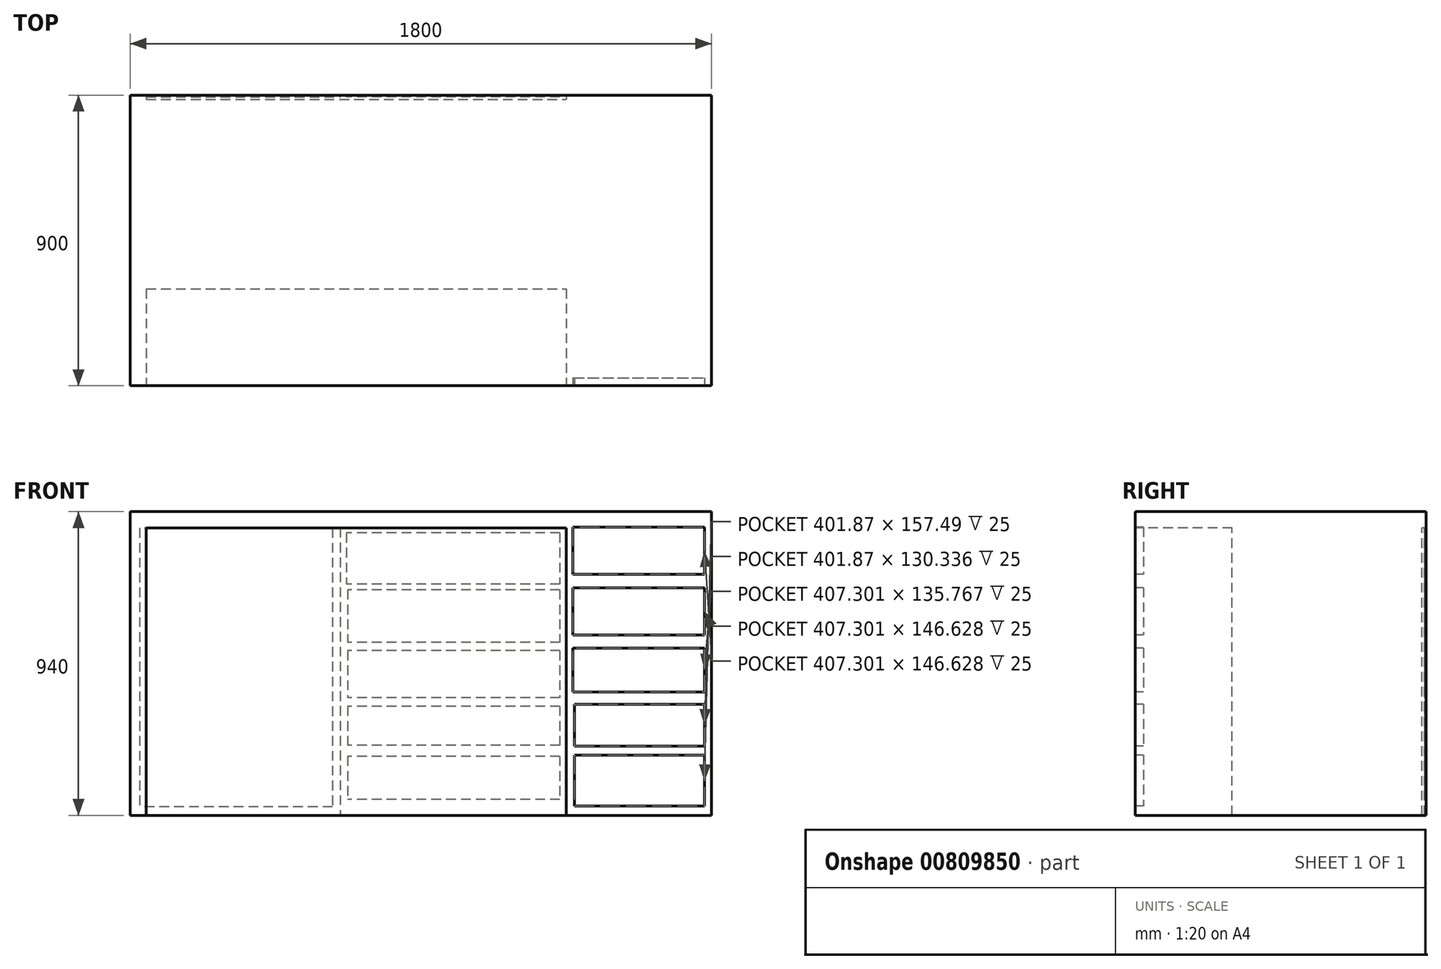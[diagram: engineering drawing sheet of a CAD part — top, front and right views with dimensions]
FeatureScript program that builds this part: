
annotation { "Feature Type Name" : "Feature", "Feature Type Description" : "" }
export const myFeature = defineFeature(function(context is Context, id is Id, definition is map)
    precondition{}
    {
        {
            var Q0;
            Q0=qCreatedBy(makeId("Front.planeOp"),FACE);
            var sketch = newSketch(context, id + "F0", { "sketchPlane" : qUnion([Q0])});
            skLineSegment(sketch, "E0.bottom", {"start": v(0, 0) * mm, "end": v(50, 0) * mm});
            skLineSegment(sketch, "E0.top", {"start": v(0, 940) * mm, "end": v(1800, 940) * mm});
            skLineSegment(sketch, "E0.left", {"start": v(0, 0) * mm, "end": v(0, 940) * mm});
            skLineSegment(sketch, "E0.right", {"start": v(1800, 0) * mm, "end": v(1800, 940) * mm});
            skLineSegment(sketch, "E1", {"start": v(50, 0) * mm, "end": v(50, 890) * mm});
            skLineSegment(sketch, "E2", {"start": v(50, 890) * mm, "end": v(1350, 890) * mm});
            skLineSegment(sketch, "E3", {"start": v(1350, 890) * mm, "end": v(1350, 0) * mm});
            skLineSegment(sketch, "E4.trimOffspring", {"start": v(1350, 0) * mm, "end": v(1800, 0) * mm});
            skSolve(sketch);
        }
        {
            var Q0;
            Q0 = qSketchRegion(id + "F0", true);
            extrude(context, id + "F1", {"entities" : qUnion([Q0]), "oppositeDirection" : true, "depth" : 900 * mm, "offsetDistance" : 25 * mm});
        }
        {
            var Q0;
            Q0=makeQuery(id+"F1.opExtrude","CAP_FACE",FACE,{"disambiguationData":[OSD([sQuery(id+"F0.wireOp",EDGE,"E0.bottom"),sQuery(id+"F0.wireOp",EDGE,"E0.top"),sQuery(id+"F0.wireOp",EDGE,"E0.left"),sQuery(id+"F0.wireOp",EDGE,"E0.right"),sQuery(id+"F0.wireOp",EDGE,"E1"),sQuery(id+"F0.wireOp",EDGE,"E2"),sQuery(id+"F0.wireOp",EDGE,"E3"),sQuery(id+"F0.wireOp",EDGE,"E4.trimOffspring")])],"isStart":true});
            var sketch = newSketch(context, id + "F2", { "sketchPlane" : qUnion([Q0])});
            skLineSegment(sketch, "E5.bottom", {"start": v(1370.64, 892.35) * mm, "end": v(1777.94, 892.35) * mm});
            skLineSegment(sketch, "E5.top", {"start": v(1370.64, 745.72) * mm, "end": v(1777.94, 745.72) * mm});
            skLineSegment(sketch, "E5.left", {"start": v(1370.64, 892.35) * mm, "end": v(1370.64, 745.72) * mm});
            skLineSegment(sketch, "E5.right", {"start": v(1777.94, 892.35) * mm, "end": v(1777.94, 745.72) * mm});
            skLineSegment(sketch, "E6.bottom", {"start": v(1370.64, 705) * mm, "end": v(1777.94, 705) * mm});
            skLineSegment(sketch, "E6.top", {"start": v(1370.64, 558.36) * mm, "end": v(1777.94, 558.36) * mm});
            skLineSegment(sketch, "E6.left", {"start": v(1370.64, 705) * mm, "end": v(1370.64, 558.36) * mm});
            skLineSegment(sketch, "E6.right", {"start": v(1777.94, 705) * mm, "end": v(1777.94, 558.36) * mm});
            skPoint(sketch, "E7.firstSnap0", {"position": v(1370.64, 631.68) * mm});
            skLineSegment(sketch, "E7.bottom", {"start": v(1370.64, 517.63) * mm, "end": v(1777.94, 517.63) * mm});
            skLineSegment(sketch, "E7.top", {"start": v(1370.64, 381.87) * mm, "end": v(1777.94, 381.87) * mm});
            skLineSegment(sketch, "E7.left", {"start": v(1370.64, 517.63) * mm, "end": v(1370.64, 381.87) * mm});
            skLineSegment(sketch, "E7.right", {"start": v(1777.94, 517.63) * mm, "end": v(1777.94, 381.87) * mm});
            skLineSegment(sketch, "E8.bottom", {"start": v(1376.07, 343.85) * mm, "end": v(1777.94, 343.85) * mm});
            skLineSegment(sketch, "E8.top", {"start": v(1376.07, 213.51) * mm, "end": v(1777.94, 213.51) * mm});
            skLineSegment(sketch, "E8.left", {"start": v(1376.07, 343.85) * mm, "end": v(1376.07, 213.51) * mm});
            skLineSegment(sketch, "E8.right", {"start": v(1777.94, 343.85) * mm, "end": v(1777.94, 213.51) * mm});
            skLineSegment(sketch, "E9.bottom", {"start": v(1376.07, 186.36) * mm, "end": v(1777.94, 186.36) * mm});
            skLineSegment(sketch, "E9.top", {"start": v(1376.07, 28.87) * mm, "end": v(1777.94, 28.87) * mm});
            skLineSegment(sketch, "E9.left", {"start": v(1376.07, 186.36) * mm, "end": v(1376.07, 28.87) * mm});
            skLineSegment(sketch, "E9.right", {"start": v(1777.94, 186.36) * mm, "end": v(1777.94, 28.87) * mm});
            skSolve(sketch);
        }
        {
            var Q0;
            Q0 = qSketchRegion(id + "F2", true);
            extrude(context, id + "F3", {"entities" : qUnion([Q0]), "operationType" : NewBodyOperationType.REMOVE, "oppositeDirection" : true, "depth" : 25 * mm, "offsetDistance" : 25 * mm});
        }
        {
            var Q0;
            Q0=makeQuery(id+"F1.opExtrude","SWEPT_FACE",FACE,{"disambiguationData":[OSD([sQuery(id+"F0.wireOp",EDGE,"E2")])]});
            var sketch = newSketch(context, id + "F4", { "sketchPlane" : qUnion([Q0])});
            skLineSegment(sketch, "E10", {"start": v(50, -300) * mm, "end": v(1350, -300) * mm});
            skLineSegment(sketch, "E11", {"start": v(50, -336.12) * mm, "end": v(1350, -336.12) * mm});
            skSolve(sketch);
        }
        {
            var Q0;
            {var subQ0=sQuery(id+"F4.wireOp",EDGE,"E10");Q0=makeQuery(id+"F4.imprint","IMPRINT",FACE,{"disambiguationData":[TD([[makeQuery(id+"F4.imprint","IMPRINT",EDGE,{"derivedFrom":subQ0}),-1.0]])]});}
            var Q1;
            Q1=makeQuery(id+"F1.opExtrude","SWEPT_FACE",FACE,{"disambiguationData":[OSD([sQuery(id+"F0.wireOp",EDGE,"E4.trimOffspring")])]});
            extrude(context, id + "F5", {"entities" : qUnion([Q0]), "operationType" : NewBodyOperationType.ADD, "endBound" : BoundingType.UP_TO_SURFACE, "depth" : 25 * mm, "endBoundEntityFace" : qUnion([Q1]), "offsetDistance" : 25 * mm});
        }
        {
            var Q0;
            Q0=makeQuery(id+"F5.opExtrude","SWEPT_FACE",FACE,{"disambiguationData":[OSD([sQuery(id+"F4.wireOp",EDGE,"E11")])]});
            var sketch = newSketch(context, id + "F6", { "sketchPlane" : qUnion([Q0])});
            skLineSegment(sketch, "E12.bottom", {"start": v(-50, 890) * mm, "end": v(-650, 890) * mm});
            skLineSegment(sketch, "E12.top", {"start": v(-50, 0) * mm, "end": v(-650, 0) * mm});
            skLineSegment(sketch, "E12.left", {"start": v(-50, 890) * mm, "end": v(-50, 0) * mm});
            skLineSegment(sketch, "E12.right", {"start": v(-650, 890) * mm, "end": v(-650, 0) * mm});
            skSolve(sketch);
        }
        {
            var Q0;
            Q0=makeQuery(id+"F6.imprint","IMPRINT",FACE,{"disambiguationData":[TD([[makeQuery(id+"F6.imprint","IMPRINT",EDGE,{"derivedFrom":sQuery(id+"F6.wireOp",EDGE,"E12.bottom")}),1.0]])]});
            extrude(context, id + "F7", {"entities" : qUnion([Q0]), "operationType" : NewBodyOperationType.ADD, "depth" : 551 * mm, "offsetDistance" : 25 * mm});
        }
        {
            var Q0;
            Q0=makeQuery(id+"F5.opExtrude","SWEPT_FACE",FACE,{"disambiguationData":[OSD([sQuery(id+"F4.wireOp",EDGE,"E11")])]});
            var Q1;
            Q1=makeQuery(id+"F7.opExtrude","CAP_FACE",FACE,{"disambiguationData":[OSD([sQuery(id+"F6.wireOp",EDGE,"E12.bottom"),sQuery(id+"F6.wireOp",EDGE,"E12.top"),sQuery(id+"F6.wireOp",EDGE,"E12.left"),sQuery(id+"F6.wireOp",EDGE,"E12.right")])],"isStart":false});
            extrude(context, id + "F8", {"entities" : qUnion([Q0]), "operationType" : NewBodyOperationType.ADD, "endBound" : BoundingType.UP_TO_SURFACE, "depth" : 540 * mm, "endBoundEntityFace" : qUnion([Q1]), "offsetDistance" : 25 * mm});
        }
        {
            var Q0;
            Q0=makeQuery(id+"F1.opExtrude","CAP_FACE",FACE,{"disambiguationData":[OSD([sQuery(id+"F0.wireOp",EDGE,"E0.bottom"),sQuery(id+"F0.wireOp",EDGE,"E0.top"),sQuery(id+"F0.wireOp",EDGE,"E0.left"),sQuery(id+"F0.wireOp",EDGE,"E0.right"),sQuery(id+"F0.wireOp",EDGE,"E1"),sQuery(id+"F0.wireOp",EDGE,"E2"),sQuery(id+"F0.wireOp",EDGE,"E3"),sQuery(id+"F0.wireOp",EDGE,"E4.trimOffspring")])],"isStart":false});
            var sketch = newSketch(context, id + "F9", { "sketchPlane" : qUnion([Q0])});
            skLineSegment(sketch, "E13.bottom", {"start": v(-50, 890) * mm, "end": v(-650, 890) * mm});
            skLineSegment(sketch, "E13.top", {"start": v(-50, 0) * mm, "end": v(-650, 0) * mm});
            skLineSegment(sketch, "E13.left", {"start": v(-50, 890) * mm, "end": v(-50, 0) * mm});
            skLineSegment(sketch, "E13.right", {"start": v(-650, 890) * mm, "end": v(-650, 0) * mm});
            skLineSegment(sketch, "E14.bottom", {"start": v(-1330.47, 874.3) * mm, "end": v(-668.82, 874.3) * mm});
            skLineSegment(sketch, "E14.top", {"start": v(-1330.47, 715.16) * mm, "end": v(-668.82, 715.16) * mm});
            skLineSegment(sketch, "E14.left", {"start": v(-1330.47, 874.3) * mm, "end": v(-1330.47, 715.16) * mm});
            skLineSegment(sketch, "E14.right", {"start": v(-668.82, 874.3) * mm, "end": v(-668.82, 715.16) * mm});
            skLineSegment(sketch, "E15.bottom", {"start": v(-1330.47, 698.41) * mm, "end": v(-673.01, 698.41) * mm});
            skLineSegment(sketch, "E15.top", {"start": v(-1330.47, 535.1) * mm, "end": v(-673.01, 535.1) * mm});
            skLineSegment(sketch, "E15.left", {"start": v(-1330.47, 698.41) * mm, "end": v(-1330.47, 535.1) * mm});
            skLineSegment(sketch, "E15.right", {"start": v(-673.01, 698.41) * mm, "end": v(-673.01, 535.1) * mm});
            skLineSegment(sketch, "E16.bottom", {"start": v(-1330.47, 509.97) * mm, "end": v(-673.01, 509.97) * mm});
            skLineSegment(sketch, "E16.top", {"start": v(-1330.47, 363.4) * mm, "end": v(-673.01, 363.4) * mm});
            skLineSegment(sketch, "E16.left", {"start": v(-1330.47, 509.97) * mm, "end": v(-1330.47, 363.4) * mm});
            skLineSegment(sketch, "E16.right", {"start": v(-673.01, 509.97) * mm, "end": v(-673.01, 363.4) * mm});
            skLineSegment(sketch, "E17.bottom", {"start": v(-1330.47, 337.74) * mm, "end": v(-673.01, 337.74) * mm});
            skLineSegment(sketch, "E17.top", {"start": v(-1330.47, 216.3) * mm, "end": v(-673.01, 216.3) * mm});
            skLineSegment(sketch, "E17.left", {"start": v(-1330.47, 337.74) * mm, "end": v(-1330.47, 216.3) * mm});
            skLineSegment(sketch, "E17.right", {"start": v(-673.01, 337.74) * mm, "end": v(-673.01, 216.3) * mm});
            skLineSegment(sketch, "E18.bottom", {"start": v(-1330.47, 182.8) * mm, "end": v(-673.01, 182.8) * mm});
            skLineSegment(sketch, "E18.top", {"start": v(-1330.47, 48.8) * mm, "end": v(-673.01, 48.8) * mm});
            skLineSegment(sketch, "E18.left", {"start": v(-1330.47, 182.8) * mm, "end": v(-1330.47, 48.8) * mm});
            skLineSegment(sketch, "E18.right", {"start": v(-673.01, 182.8) * mm, "end": v(-673.01, 48.8) * mm});
            skSolve(sketch);
        }
        {
            var Q0;
            Q0 = qSketchRegion(id + "F9", true);
            extrude(context, id + "F10", {"entities" : qUnion([Q0]), "operationType" : NewBodyOperationType.ADD, "oppositeDirection" : true, "depth" : 5 * mm, "offsetDistance" : 25 * mm});
        }
        {
            var Q0;
            Q0=makeQuery(id+"F10.boolean.opBoolean","MERGE",FACE,{"derivedFrom":[makeQuery(id+"F1.opExtrude","CAP_FACE",FACE,{"disambiguationData":[OSD([sQuery(id+"F0.wireOp",EDGE,"E0.bottom"),sQuery(id+"F0.wireOp",EDGE,"E0.top"),sQuery(id+"F0.wireOp",EDGE,"E0.left"),sQuery(id+"F0.wireOp",EDGE,"E0.right"),sQuery(id+"F0.wireOp",EDGE,"E1"),sQuery(id+"F0.wireOp",EDGE,"E2"),sQuery(id+"F0.wireOp",EDGE,"E3"),sQuery(id+"F0.wireOp",EDGE,"E4.trimOffspring")])],"isStart":false}),makeQuery(id+"F10.opExtrude","CAP_FACE",FACE,{"disambiguationData":[OSD([sQuery(id+"F9.wireOp",EDGE,"E13.bottom"),sQuery(id+"F9.wireOp",EDGE,"E13.top"),sQuery(id+"F9.wireOp",EDGE,"E13.left"),sQuery(id+"F9.wireOp",EDGE,"E13.right")])],"isStart":true})]});
            var sketch = newSketch(context, id + "F11", { "sketchPlane" : qUnion([Q0])});
            skLineSegment(sketch, "E19.bottom", {"start": v(-626.68, 889.34) * mm, "end": v(-29.3, 889.34) * mm});
            skLineSegment(sketch, "E19.top", {"start": v(-626.68, 25.87) * mm, "end": v(-29.3, 25.87) * mm});
            skLineSegment(sketch, "E19.left", {"start": v(-626.68, 889.34) * mm, "end": v(-626.68, 25.87) * mm});
            skLineSegment(sketch, "E19.right", {"start": v(-29.3, 889.34) * mm, "end": v(-29.3, 25.87) * mm});
            skSolve(sketch);
        }
        {
            var Q0;
            Q0=makeQuery(id+"F11.imprint","IMPRINT",FACE,{"disambiguationData":[TD([[makeQuery(id+"F11.imprint","IMPRINT",EDGE,{"derivedFrom":sQuery(id+"F11.wireOp",EDGE,"E19.bottom")}),-1.0]])]});
            extrude(context, id + "F12", {"entities" : qUnion([Q0]), "operationType" : NewBodyOperationType.REMOVE, "oppositeDirection" : true, "depth" : 2 * mm, "offsetDistance" : 25 * mm});
        }
    });
